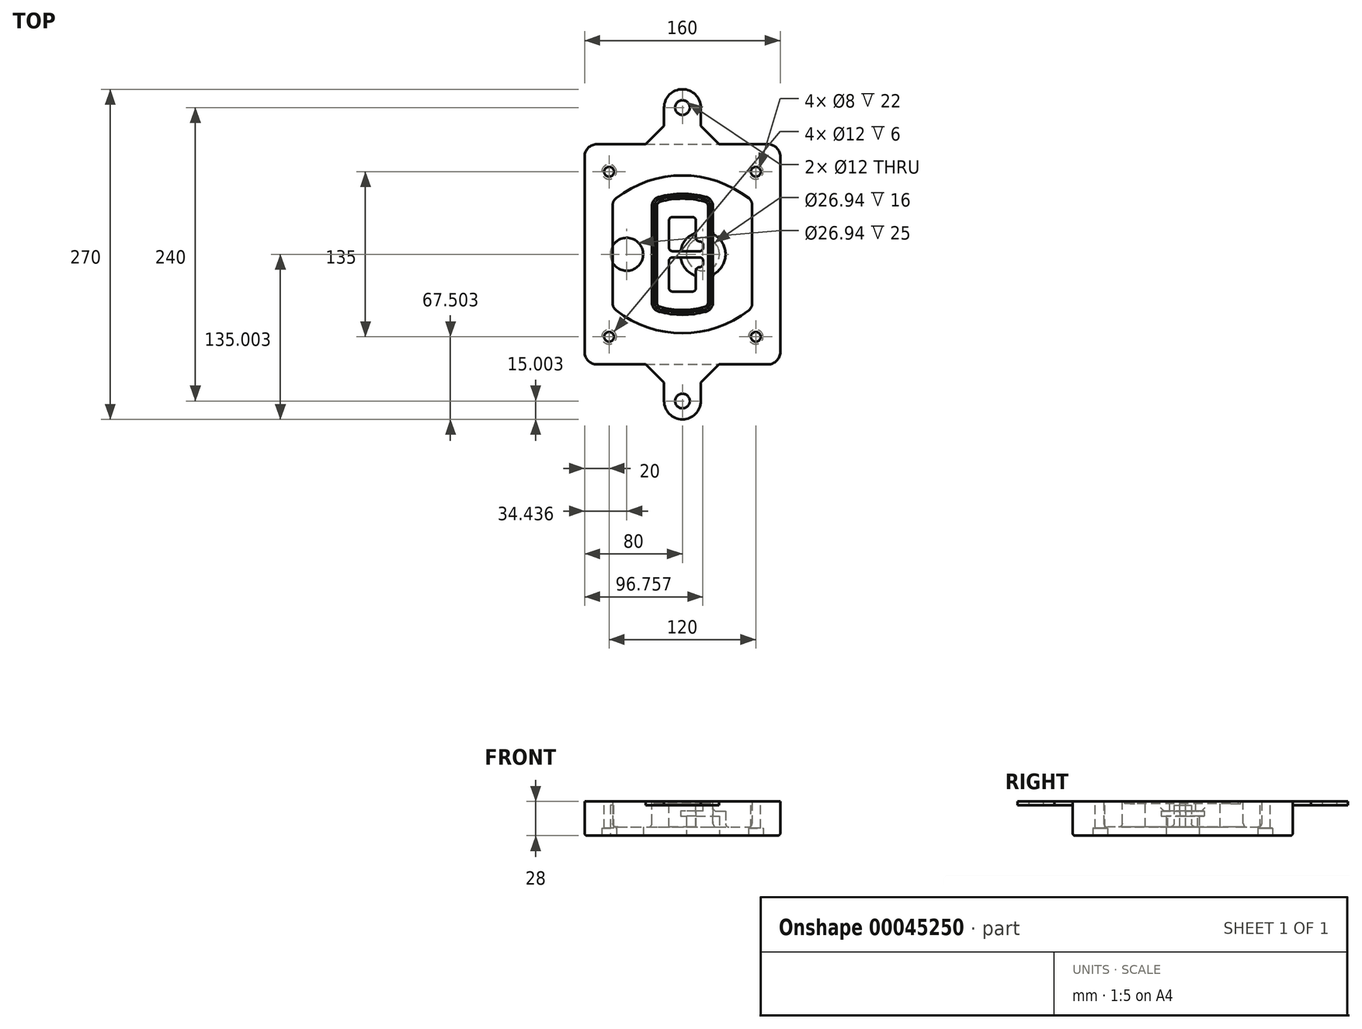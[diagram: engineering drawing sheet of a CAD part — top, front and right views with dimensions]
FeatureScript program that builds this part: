
annotation { "Feature Type Name" : "Feature", "Feature Type Description" : "" }
export const myFeature = defineFeature(function(context is Context, id is Id, definition is map)
    precondition{}
    {
        {
            var Q0;
            Q0=qCreatedBy(makeId("Top.planeOp"),FACE);
            var sketch = newSketch(context, id + "F0", { "sketchPlane" : qUnion([Q0])});
            skPoint(sketch, "E0.rect.middle", {"position": v(0, 0) * mm});
            skLineSegment(sketch, "E1.bottom", {"start": v(24.05, 28.38) * mm, "end": v(164.05, 28.38) * mm});
            skLineSegment(sketch, "E1.top", {"start": v(24.05, 208.38) * mm, "end": v(164.05, 208.38) * mm});
            skLineSegment(sketch, "E1.left", {"start": v(14.05, 38.38) * mm, "end": v(14.05, 198.38) * mm});
            skLineSegment(sketch, "E1.right", {"start": v(174.05, 38.38) * mm, "end": v(174.05, 198.38) * mm});
            skLineSegment(sketch, "E2", {"start": v(14.05, 208.38) * mm, "end": v(174.05, 28.38) * mm, "construction": true});
            skLineSegment(sketch, "E3", {"start": v(174.05, 208.38) * mm, "end": v(14.05, 28.38) * mm, "construction": true});
            skCircle(sketch, "E4", {"center": v(34.05, 185.88) * mm, "radius": 4 * mm});
            skCircle(sketch, "E5", {"center": v(154.05, 185.88) * mm, "radius": 4 * mm});
            skCircle(sketch, "E6", {"center": v(154.05, 50.88) * mm, "radius": 4 * mm});
            skCircle(sketch, "E7", {"center": v(34.05, 50.88) * mm, "radius": 4 * mm});
            skLineSegment(sketch, "E8", {"start": v(34.05, 185.88) * mm, "end": v(154.05, 185.88) * mm, "construction": true});
            skLineSegment(sketch, "E9", {"start": v(154.05, 185.88) * mm, "end": v(154.05, 50.88) * mm, "construction": true});
            skLineSegment(sketch, "E10", {"start": v(154.05, 50.88) * mm, "end": v(34.05, 50.88) * mm, "construction": true});
            skLineSegment(sketch, "E11", {"start": v(34.05, 50.88) * mm, "end": v(34.05, 185.88) * mm, "construction": true});
            skLineSegment(sketch, "E12", {"start": v(34.05, 158.68) * mm, "end": v(34.05, 78.09) * mm});
            skLineSegment(sketch, "E13", {"start": v(154.05, 158.68) * mm, "end": v(154.05, 78.09) * mm});
            skArc(sketch, "E14", {"start": v(150.2, 166.56) * mm, "mid": v(94.05, 185.88) * mm, "end": v(37.9, 166.56) * mm});
            skArc(sketch, "E15", {"start": v(37.9, 70.2) * mm, "mid": v(94.05, 50.88) * mm, "end": v(150.2, 70.2) * mm});
            skLineSegment(sketch, "E16", {"start": v(34.05, 118.38) * mm, "end": v(154.05, 118.38) * mm, "construction": true});
            skPoint(sketch, "E17.visualSharp", {"position": v(34.05, 73.38) * mm});
            skArc(sketch, "E17.filletArc", {"start": v(34.05, 78.09) * mm, "mid": v(35.06, 73.7) * mm, "end": v(37.9, 70.2) * mm});
            skPoint(sketch, "E18.visualSharp", {"position": v(34.05, 163.38) * mm});
            skArc(sketch, "E18.filletArc", {"start": v(37.9, 166.56) * mm, "mid": v(35.06, 163.06) * mm, "end": v(34.05, 158.68) * mm});
            skPoint(sketch, "E19.visualSharp", {"position": v(154.05, 163.38) * mm});
            skArc(sketch, "E19.filletArc", {"start": v(154.05, 158.68) * mm, "mid": v(153.04, 163.06) * mm, "end": v(150.2, 166.56) * mm});
            skPoint(sketch, "E20.visualSharp", {"position": v(154.05, 73.38) * mm});
            skArc(sketch, "E20.filletArc", {"start": v(150.2, 70.2) * mm, "mid": v(153.04, 73.7) * mm, "end": v(154.05, 78.09) * mm});
            skPoint(sketch, "E21.visualSharp", {"position": v(14.05, 208.38) * mm});
            skArc(sketch, "E21.filletArc", {"start": v(24.05, 208.38) * mm, "mid": v(16.98, 205.45) * mm, "end": v(14.05, 198.38) * mm});
            skPoint(sketch, "E22.visualSharp", {"position": v(174.05, 208.38) * mm});
            skArc(sketch, "E22.filletArc", {"start": v(174.05, 198.38) * mm, "mid": v(171.12, 205.45) * mm, "end": v(164.05, 208.38) * mm});
            skPoint(sketch, "E23.visualSharp", {"position": v(174.05, 28.38) * mm});
            skArc(sketch, "E23.filletArc", {"start": v(164.05, 28.38) * mm, "mid": v(171.12, 31.31) * mm, "end": v(174.05, 38.38) * mm});
            skPoint(sketch, "E24.visualSharp", {"position": v(14.05, 28.38) * mm});
            skArc(sketch, "E24.filletArc", {"start": v(14.05, 38.38) * mm, "mid": v(16.98, 31.31) * mm, "end": v(24.05, 28.38) * mm});
            skArc(sketch, "E25.0", {"start": v(151.05, 158.68) * mm, "mid": v(150.34, 161.75) * mm, "end": v(148.36, 164.2) * mm});
            skLineSegment(sketch, "E25.1", {"start": v(151.05, 158.68) * mm, "end": v(151.05, 78.09) * mm});
            skArc(sketch, "E25.2", {"start": v(148.36, 72.57) * mm, "mid": v(150.34, 75.02) * mm, "end": v(151.05, 78.09) * mm});
            skArc(sketch, "E25.3", {"start": v(39.74, 72.57) * mm, "mid": v(94.05, 53.88) * mm, "end": v(148.36, 72.57) * mm});
            skArc(sketch, "E25.4", {"start": v(37.05, 78.09) * mm, "mid": v(37.76, 75.02) * mm, "end": v(39.74, 72.57) * mm});
            skArc(sketch, "E25.5", {"start": v(148.36, 164.2) * mm, "mid": v(94.05, 182.88) * mm, "end": v(39.74, 164.2) * mm});
            skLineSegment(sketch, "E25.6", {"start": v(37.05, 158.68) * mm, "end": v(37.05, 78.09) * mm});
            skArc(sketch, "E25.7", {"start": v(39.74, 164.2) * mm, "mid": v(37.76, 161.75) * mm, "end": v(37.05, 158.68) * mm});
            skArc(sketch, "E26.0", {"start": v(35.43, 169.71) * mm, "mid": v(31.47, 164.82) * mm, "end": v(30.05, 158.68) * mm});
            skArc(sketch, "E26.1", {"start": v(152.67, 169.71) * mm, "mid": v(94.05, 189.88) * mm, "end": v(35.43, 169.71) * mm});
            skArc(sketch, "E26.2", {"start": v(158.05, 158.68) * mm, "mid": v(156.63, 164.82) * mm, "end": v(152.67, 169.71) * mm});
            skLineSegment(sketch, "E26.3", {"start": v(158.05, 158.68) * mm, "end": v(158.05, 78.09) * mm});
            skArc(sketch, "E26.4", {"start": v(152.67, 67.05) * mm, "mid": v(156.63, 71.95) * mm, "end": v(158.05, 78.09) * mm});
            skLineSegment(sketch, "E26.5", {"start": v(30.05, 158.68) * mm, "end": v(30.05, 78.09) * mm});
            skArc(sketch, "E26.6", {"start": v(35.43, 67.05) * mm, "mid": v(94.05, 46.88) * mm, "end": v(152.67, 67.05) * mm});
            skArc(sketch, "E26.7", {"start": v(30.05, 78.09) * mm, "mid": v(31.47, 71.95) * mm, "end": v(35.43, 67.05) * mm});
            skSolve(sketch);
        }
        {
            var Q0;
            Q0=makeQuery(id+"F0.imprint","IMPRINT",FACE,{"disambiguationData":[TD([[makeQuery(id+"F0.imprint","IMPRINT",EDGE,{"derivedFrom":sQuery(id+"F0.wireOp",EDGE,"E1.bottom")}),1.0]])]});
            var Q1;
            Q1=makeQuery(id+"F0.imprint","IMPRINT",FACE,{"disambiguationData":[TD([[makeQuery(id+"F0.imprint","IMPRINT",EDGE,{"derivedFrom":sQuery(id+"F0.wireOp",EDGE,"E12")}),1.0]])]});
            var Q2;
            Q2=makeQuery(id+"F0.imprint","IMPRINT",FACE,{"disambiguationData":[TD([[makeQuery(id+"F0.imprint","IMPRINT",EDGE,{"derivedFrom":sQuery(id+"F0.wireOp",EDGE,"E25.0")}),1.0]])]});
            var Q3;
            Q3=makeQuery(id+"F0.imprint","IMPRINT",FACE,{"disambiguationData":[TD([[makeQuery(id+"F0.imprint","IMPRINT",EDGE,{"derivedFrom":sQuery(id+"F0.wireOp",EDGE,"E12")}),-1.0]])]});
            extrude(context, id + "F1", {"entities" : qUnion([Q0, Q1, Q2, Q3]), "oppositeDirection" : true, "depth" : 25 * mm});
        }
        {
            var Q0;
            Q0=makeQuery(id+"F0.imprint","IMPRINT",FACE,{"disambiguationData":[TD([[makeQuery(id+"F0.imprint","IMPRINT",EDGE,{"derivedFrom":sQuery(id+"F0.wireOp",EDGE,"E12")}),1.0]])]});
            extrude(context, id + "F2", {"entities" : qUnion([Q0]), "operationType" : NewBodyOperationType.ADD, "depth" : 3 * mm});
        }
        {
            var Q0;
            Q0=makeQuery(id+"F0.imprint","IMPRINT",FACE,{"disambiguationData":[TD([[makeQuery(id+"F0.imprint","IMPRINT",EDGE,{"derivedFrom":sQuery(id+"F0.wireOp",EDGE,"E25.0")}),1.0]])]});
            extrude(context, id + "F3", {"entities" : qUnion([Q0]), "operationType" : NewBodyOperationType.REMOVE, "oppositeDirection" : true, "depth" : 18 * mm});
        }
        {
            var Q0;
            Q0=makeQuery(id+"F2.opExtrude","CAP_FACE",FACE,{"disambiguationData":[OSD([sQuery(id+"F0.wireOp",EDGE,"E12"),sQuery(id+"F0.wireOp",EDGE,"E13"),sQuery(id+"F0.wireOp",EDGE,"E14"),sQuery(id+"F0.wireOp",EDGE,"E15"),sQuery(id+"F0.wireOp",EDGE,"E17.filletArc"),sQuery(id+"F0.wireOp",EDGE,"E18.filletArc"),sQuery(id+"F0.wireOp",EDGE,"E19.filletArc"),sQuery(id+"F0.wireOp",EDGE,"E20.filletArc"),sQuery(id+"F0.wireOp",EDGE,"E25.0"),sQuery(id+"F0.wireOp",EDGE,"E25.1"),sQuery(id+"F0.wireOp",EDGE,"E25.2"),sQuery(id+"F0.wireOp",EDGE,"E25.3"),sQuery(id+"F0.wireOp",EDGE,"E25.4"),sQuery(id+"F0.wireOp",EDGE,"E25.5"),sQuery(id+"F0.wireOp",EDGE,"E25.6"),sQuery(id+"F0.wireOp",EDGE,"E25.7")])],"isStart":false});
            var sketch = newSketch(context, id + "F4", { "sketchPlane" : qUnion([Q0])});
            skArc(sketch, "E27.0", {"start": v(74.97, 71.41) * mm, "mid": v(94.05, 68.88) * mm, "end": v(113.13, 71.41) * mm});
            skArc(sketch, "E28.0", {"start": v(113.13, 165.35) * mm, "mid": v(94.05, 167.88) * mm, "end": v(74.97, 165.35) * mm});
            skLineSegment(sketch, "E29", {"start": v(69.05, 157.63) * mm, "end": v(69.05, 79.14) * mm});
            skLineSegment(sketch, "E30", {"start": v(119.05, 157.63) * mm, "end": v(119.05, 79.14) * mm});
            skLineSegment(sketch, "E31", {"start": v(69.05, 163.48) * mm, "end": v(119.05, 163.48) * mm, "construction": true});
            skLineSegment(sketch, "E32", {"start": v(69.05, 73.28) * mm, "end": v(119.05, 73.28) * mm, "construction": true});
            skPoint(sketch, "E33.visualSharp", {"position": v(69.05, 163.48) * mm});
            skArc(sketch, "E33.filletArc", {"start": v(74.97, 165.35) * mm, "mid": v(70.7, 162.5) * mm, "end": v(69.05, 157.63) * mm});
            skPoint(sketch, "E34.visualSharp", {"position": v(119.05, 163.48) * mm});
            skArc(sketch, "E34.filletArc", {"start": v(119.05, 157.63) * mm, "mid": v(117.4, 162.5) * mm, "end": v(113.13, 165.35) * mm});
            skPoint(sketch, "E35.visualSharp", {"position": v(119.05, 73.28) * mm});
            skArc(sketch, "E35.filletArc", {"start": v(113.13, 71.41) * mm, "mid": v(117.4, 74.27) * mm, "end": v(119.05, 79.14) * mm});
            skPoint(sketch, "E36.visualSharp", {"position": v(69.05, 73.28) * mm});
            skArc(sketch, "E36.filletArc", {"start": v(69.05, 79.14) * mm, "mid": v(70.7, 74.27) * mm, "end": v(74.97, 71.41) * mm});
            skArc(sketch, "E37.0", {"start": v(148.36, 164.2) * mm, "mid": v(94.05, 182.88) * mm, "end": v(39.74, 164.2) * mm});
            skArc(sketch, "E37.1", {"start": v(39.74, 164.2) * mm, "mid": v(37.76, 161.75) * mm, "end": v(37.05, 158.68) * mm});
            skLineSegment(sketch, "E37.2", {"start": v(37.05, 158.68) * mm, "end": v(37.05, 78.09) * mm});
            skArc(sketch, "E37.3", {"start": v(37.05, 78.09) * mm, "mid": v(37.76, 75.02) * mm, "end": v(39.74, 72.57) * mm});
            skArc(sketch, "E37.4", {"start": v(39.74, 72.57) * mm, "mid": v(94.05, 53.88) * mm, "end": v(148.36, 72.57) * mm});
            skArc(sketch, "E37.5", {"start": v(148.36, 72.57) * mm, "mid": v(150.34, 75.02) * mm, "end": v(151.05, 78.09) * mm});
            skLineSegment(sketch, "E37.6", {"start": v(151.05, 158.68) * mm, "end": v(151.05, 78.09) * mm});
            skArc(sketch, "E37.7", {"start": v(151.05, 158.68) * mm, "mid": v(150.34, 161.75) * mm, "end": v(148.36, 164.2) * mm});
            skLineSegment(sketch, "E38.0", {"start": v(117.05, 157.63) * mm, "end": v(117.05, 79.14) * mm});
            skArc(sketch, "E38.1", {"start": v(112.61, 73.34) * mm, "mid": v(115.81, 75.49) * mm, "end": v(117.05, 79.14) * mm});
            skArc(sketch, "E38.2", {"start": v(75.49, 73.34) * mm, "mid": v(94.05, 70.88) * mm, "end": v(112.61, 73.34) * mm});
            skArc(sketch, "E38.3", {"start": v(71.05, 79.14) * mm, "mid": v(72.29, 75.49) * mm, "end": v(75.49, 73.34) * mm});
            skLineSegment(sketch, "E38.4", {"start": v(71.05, 157.63) * mm, "end": v(71.05, 79.14) * mm});
            skArc(sketch, "E38.5", {"start": v(117.05, 157.63) * mm, "mid": v(115.81, 161.28) * mm, "end": v(112.61, 163.42) * mm});
            skArc(sketch, "E38.6", {"start": v(75.49, 163.42) * mm, "mid": v(72.29, 161.28) * mm, "end": v(71.05, 157.63) * mm});
            skArc(sketch, "E38.7", {"start": v(112.61, 163.42) * mm, "mid": v(94.05, 165.88) * mm, "end": v(75.49, 163.42) * mm});
            skArc(sketch, "E39.0", {"start": v(115.05, 157.63) * mm, "mid": v(114.23, 160.06) * mm, "end": v(112.1, 161.5) * mm});
            skLineSegment(sketch, "E39.1", {"start": v(115.05, 157.63) * mm, "end": v(115.05, 79.14) * mm});
            skArc(sketch, "E39.2", {"start": v(112.1, 75.27) * mm, "mid": v(114.23, 76.7) * mm, "end": v(115.05, 79.14) * mm});
            skArc(sketch, "E39.3", {"start": v(76, 75.27) * mm, "mid": v(94.05, 72.88) * mm, "end": v(112.1, 75.27) * mm});
            skArc(sketch, "E39.4", {"start": v(73.05, 79.14) * mm, "mid": v(73.87, 76.7) * mm, "end": v(76, 75.27) * mm});
            skArc(sketch, "E39.5", {"start": v(112.1, 161.5) * mm, "mid": v(94.05, 163.88) * mm, "end": v(76, 161.5) * mm});
            skLineSegment(sketch, "E39.6", {"start": v(73.05, 157.63) * mm, "end": v(73.05, 79.14) * mm});
            skArc(sketch, "E39.7", {"start": v(76, 161.5) * mm, "mid": v(73.87, 160.06) * mm, "end": v(73.05, 157.63) * mm});
            skLineSegment(sketch, "E40", {"start": v(69.05, 118.38) * mm, "end": v(119.05, 118.38) * mm, "construction": true});
            skLineSegment(sketch, "E41", {"start": v(83.05, 123.88) * mm, "end": v(83.05, 145.88) * mm});
            skLineSegment(sketch, "E42", {"start": v(86.05, 148.88) * mm, "end": v(102.05, 148.88) * mm});
            skLineSegment(sketch, "E43", {"start": v(105.05, 145.88) * mm, "end": v(105.05, 131.88) * mm});
            skLineSegment(sketch, "E44", {"start": v(108.05, 128.88) * mm, "end": v(108.05, 128.88) * mm});
            skLineSegment(sketch, "E45", {"start": v(111.05, 125.88) * mm, "end": v(111.05, 123.88) * mm});
            skLineSegment(sketch, "E46", {"start": v(108.05, 120.88) * mm, "end": v(86.05, 120.88) * mm});
            skPoint(sketch, "E47.visualSharp", {"position": v(83.05, 148.88) * mm});
            skArc(sketch, "E47.filletArc", {"start": v(86.05, 148.88) * mm, "mid": v(83.93, 148) * mm, "end": v(83.05, 145.88) * mm});
            skPoint(sketch, "E48.visualSharp", {"position": v(105.05, 148.88) * mm});
            skArc(sketch, "E48.filletArc", {"start": v(105.05, 145.88) * mm, "mid": v(104.17, 148) * mm, "end": v(102.05, 148.88) * mm});
            skPoint(sketch, "E49.visualSharp", {"position": v(105.05, 128.88) * mm});
            skArc(sketch, "E49.filletArc", {"start": v(105.05, 131.88) * mm, "mid": v(105.93, 129.76) * mm, "end": v(108.05, 128.88) * mm});
            skPoint(sketch, "E50.visualSharp", {"position": v(111.05, 128.88) * mm});
            skArc(sketch, "E50.filletArc", {"start": v(111.05, 125.88) * mm, "mid": v(110.17, 128) * mm, "end": v(108.05, 128.88) * mm});
            skPoint(sketch, "E51.visualSharp", {"position": v(111.05, 120.88) * mm});
            skArc(sketch, "E51.filletArc", {"start": v(108.05, 120.88) * mm, "mid": v(110.17, 121.76) * mm, "end": v(111.05, 123.88) * mm});
            skPoint(sketch, "E52.visualSharp", {"position": v(83.05, 120.88) * mm});
            skArc(sketch, "E52.filletArc", {"start": v(83.05, 123.88) * mm, "mid": v(83.93, 121.76) * mm, "end": v(86.05, 120.88) * mm});
            skLineSegment(sketch, "E53.0.MirrorCS", {"start": v(108.05, 115.88) * mm, "end": v(86.05, 115.88) * mm});
            skArc(sketch, "E54.0.MirrorCS", {"start": v(83.05, 112.88) * mm, "mid": v(83.93, 115) * mm, "end": v(86.05, 115.88) * mm});
            skLineSegment(sketch, "E55.0.MirrorCS", {"start": v(83.05, 112.88) * mm, "end": v(83.05, 90.88) * mm});
            skArc(sketch, "E56.0.MirrorCS", {"start": v(86.05, 87.88) * mm, "mid": v(83.93, 88.76) * mm, "end": v(83.05, 90.88) * mm});
            skLineSegment(sketch, "E57.0.MirrorCS", {"start": v(86.05, 87.88) * mm, "end": v(102.05, 87.88) * mm});
            skArc(sketch, "E58.0.MirrorCS", {"start": v(105.05, 90.88) * mm, "mid": v(104.17, 88.76) * mm, "end": v(102.05, 87.88) * mm});
            skLineSegment(sketch, "E59.0.MirrorCS", {"start": v(105.05, 90.88) * mm, "end": v(105.05, 104.88) * mm});
            skArc(sketch, "E60.0.MirrorCS", {"start": v(105.05, 104.88) * mm, "mid": v(105.93, 107) * mm, "end": v(108.05, 107.88) * mm});
            skArc(sketch, "E61.0.MirrorCS", {"start": v(111.05, 110.88) * mm, "mid": v(110.17, 108.76) * mm, "end": v(108.05, 107.88) * mm});
            skLineSegment(sketch, "E62.0.MirrorCS", {"start": v(111.05, 110.88) * mm, "end": v(111.05, 112.88) * mm});
            skArc(sketch, "E63.0.MirrorCS", {"start": v(108.05, 115.88) * mm, "mid": v(110.17, 115) * mm, "end": v(111.05, 112.88) * mm});
            skSolve(sketch);
        }
        {
            var Q0;
            Q0=makeQuery(id+"F4.imprint","IMPRINT",FACE,{"disambiguationData":[TD([[makeQuery(id+"F4.imprint","IMPRINT",EDGE,{"derivedFrom":sQuery(id+"F4.wireOp",EDGE,"E27.0")}),1.0]])]});
            var Q1;
            Q1=makeQuery(id+"F4.imprint","IMPRINT",FACE,{"disambiguationData":[TD([[makeQuery(id+"F4.imprint","IMPRINT",EDGE,{"derivedFrom":sQuery(id+"F4.wireOp",EDGE,"E38.0")}),-1.0]])]});
            var Q2;
            Q2=makeQuery(id+"F4.imprint","IMPRINT",FACE,{"disambiguationData":[TD([[makeQuery(id+"F4.imprint","IMPRINT",EDGE,{"derivedFrom":sQuery(id+"F4.wireOp",EDGE,"E39.0")}),1.0]])]});
            extrude(context, id + "F5", {"entities" : qUnion([Q0, Q1, Q2]), "operationType" : NewBodyOperationType.ADD, "endBound" : BoundingType.UP_TO_NEXT, "oppositeDirection" : true, "depth" : 25 * mm});
        }
        {
            var Q0;
            Q0=makeQuery(id+"F4.imprint","IMPRINT",FACE,{"disambiguationData":[TD([[makeQuery(id+"F4.imprint","IMPRINT",EDGE,{"derivedFrom":sQuery(id+"F4.wireOp",EDGE,"E38.0")}),-1.0]])]});
            extrude(context, id + "F6", {"entities" : qUnion([Q0]), "operationType" : NewBodyOperationType.REMOVE, "oppositeDirection" : true, "depth" : 2 * mm});
        }
        {
            var Q0;
            Q0=makeQuery(id+"F1.opExtrude","CAP_FACE",FACE,{"disambiguationData":[OSD([sQuery(id+"F0.wireOp",EDGE,"E1.bottom"),sQuery(id+"F0.wireOp",EDGE,"E1.top"),sQuery(id+"F0.wireOp",EDGE,"E1.left"),sQuery(id+"F0.wireOp",EDGE,"E1.right"),sQuery(id+"F0.wireOp",EDGE,"E4"),sQuery(id+"F0.wireOp",EDGE,"E5"),sQuery(id+"F0.wireOp",EDGE,"E6"),sQuery(id+"F0.wireOp",EDGE,"E7"),sQuery(id+"F0.wireOp",EDGE,"E21.filletArc"),sQuery(id+"F0.wireOp",EDGE,"E22.filletArc"),sQuery(id+"F0.wireOp",EDGE,"E23.filletArc"),sQuery(id+"F0.wireOp",EDGE,"E24.filletArc")])],"isStart":false});
            var sketch = newSketch(context, id + "F7", { "sketchPlane" : qUnion([Q0])});
            skCircle(sketch, "E64", {"center": v(110.8, -118.38) * mm, "radius": 13.47 * mm});
            skCircle(sketch, "E65", {"center": v(48.49, -118.38) * mm, "radius": 13.47 * mm});
            skLineSegment(sketch, "E66", {"start": v(174.05, -118.38) * mm, "end": v(14.05, -118.38) * mm});
            skCircle(sketch, "E67", {"center": v(110.8, -118.38) * mm, "radius": 18.47 * mm});
            skCircle(sketch, "E68", {"center": v(154.05, -185.88) * mm, "radius": 6 * mm});
            skCircle(sketch, "E69", {"center": v(34.05, -185.88) * mm, "radius": 6 * mm});
            skCircle(sketch, "E70", {"center": v(34.05, -50.88) * mm, "radius": 6 * mm});
            skCircle(sketch, "E71", {"center": v(154.05, -50.88) * mm, "radius": 6 * mm});
            skSolve(sketch);
        }
        {
            var Q0;
            {var subQ1=sQuery(id+"F7.wireOp",EDGE,"E66");var subQ4=sQuery(id+"F7.wireOp",EDGE,"E64");var subQ6=makeQuery(id+"F7.imprint","INTERSECT",VERTEX,{"disambiguationData":[OD(0.0)],"derivedFrom":[subQ4,subQ1]});Q0=makeQuery(id+"F7.imprint","IMPRINT",FACE,{"disambiguationData":[TD([[makeQuery(id+"F7.imprint","IMPRINT",EDGE,{"disambiguationData":[TD([[subQ6,-1.0]])],"derivedFrom":subQ4}),-1.0]])]});}
            var Q1;
            {var subQ0=sQuery(id+"F7.wireOp",EDGE,"E66");var subQ1=sQuery(id+"F7.wireOp",EDGE,"E64");var subQ3=makeQuery(id+"F7.imprint","INTERSECT",VERTEX,{"disambiguationData":[OD(0.0)],"derivedFrom":[subQ1,subQ0]});Q1=makeQuery(id+"F7.imprint","IMPRINT",FACE,{"disambiguationData":[TD([[makeQuery(id+"F7.imprint","IMPRINT",EDGE,{"disambiguationData":[TD([[subQ3,-1.0]])],"derivedFrom":subQ1}),1.0]])]});}
            var Q2;
            {var subQ0=sQuery(id+"F7.wireOp",EDGE,"E66");var subQ1=sQuery(id+"F7.wireOp",EDGE,"E64");var subQ3=makeQuery(id+"F7.imprint","INTERSECT",VERTEX,{"disambiguationData":[OD(0.0)],"derivedFrom":[subQ1,subQ0]});Q2=makeQuery(id+"F7.imprint","IMPRINT",FACE,{"disambiguationData":[TD([[makeQuery(id+"F7.imprint","IMPRINT",EDGE,{"disambiguationData":[TD([[subQ3,1.0]])],"derivedFrom":subQ1}),1.0]])]});}
            var Q3;
            {var subQ1=sQuery(id+"F7.wireOp",EDGE,"E66");var subQ4=sQuery(id+"F7.wireOp",EDGE,"E64");var subQ6=makeQuery(id+"F7.imprint","INTERSECT",VERTEX,{"disambiguationData":[OD(0.0)],"derivedFrom":[subQ4,subQ1]});Q3=makeQuery(id+"F7.imprint","IMPRINT",FACE,{"disambiguationData":[TD([[makeQuery(id+"F7.imprint","IMPRINT",EDGE,{"disambiguationData":[TD([[subQ6,1.0]])],"derivedFrom":subQ4}),-1.0]])]});}
            extrude(context, id + "F8", {"entities" : qUnion([Q0, Q1, Q2, Q3]), "operationType" : NewBodyOperationType.ADD, "oppositeDirection" : true, "depth" : 20 * mm});
        }
        {
            var Q0;
            {var subQ0=sQuery(id+"F7.wireOp",EDGE,"E66");var subQ1=sQuery(id+"F7.wireOp",EDGE,"E64");var subQ3=makeQuery(id+"F7.imprint","INTERSECT",VERTEX,{"disambiguationData":[OD(0.0)],"derivedFrom":[subQ1,subQ0]});Q0=makeQuery(id+"F7.imprint","IMPRINT",FACE,{"disambiguationData":[TD([[makeQuery(id+"F7.imprint","IMPRINT",EDGE,{"disambiguationData":[TD([[subQ3,-1.0]])],"derivedFrom":subQ1}),1.0]])]});}
            var Q1;
            {var subQ0=sQuery(id+"F7.wireOp",EDGE,"E66");var subQ1=sQuery(id+"F7.wireOp",EDGE,"E64");var subQ3=makeQuery(id+"F7.imprint","INTERSECT",VERTEX,{"disambiguationData":[OD(0.0)],"derivedFrom":[subQ1,subQ0]});Q1=makeQuery(id+"F7.imprint","IMPRINT",FACE,{"disambiguationData":[TD([[makeQuery(id+"F7.imprint","IMPRINT",EDGE,{"disambiguationData":[TD([[subQ3,1.0]])],"derivedFrom":subQ1}),1.0]])]});}
            extrude(context, id + "F9", {"entities" : qUnion([Q0, Q1]), "operationType" : NewBodyOperationType.REMOVE, "oppositeDirection" : true, "depth" : 16 * mm});
        }
        {
            var Q0;
            {var subQ0=sQuery(id+"F7.wireOp",EDGE,"E66");var subQ1=sQuery(id+"F7.wireOp",EDGE,"E65");var subQ3=makeQuery(id+"F7.imprint","INTERSECT",VERTEX,{"disambiguationData":[OD(0.0)],"derivedFrom":[subQ1,subQ0]});Q0=makeQuery(id+"F7.imprint","IMPRINT",FACE,{"disambiguationData":[TD([[makeQuery(id+"F7.imprint","IMPRINT",EDGE,{"disambiguationData":[TD([[subQ3,-1.0]])],"derivedFrom":subQ1}),1.0]])]});}
            var Q1;
            {var subQ0=sQuery(id+"F7.wireOp",EDGE,"E66");var subQ1=sQuery(id+"F7.wireOp",EDGE,"E65");var subQ3=makeQuery(id+"F7.imprint","INTERSECT",VERTEX,{"disambiguationData":[OD(0.0)],"derivedFrom":[subQ1,subQ0]});Q1=makeQuery(id+"F7.imprint","IMPRINT",FACE,{"disambiguationData":[TD([[makeQuery(id+"F7.imprint","IMPRINT",EDGE,{"disambiguationData":[TD([[subQ3,1.0]])],"derivedFrom":subQ1}),1.0]])]});}
            extrude(context, id + "F10", {"entities" : qUnion([Q0, Q1]), "operationType" : NewBodyOperationType.REMOVE, "oppositeDirection" : true, "depth" : 25 * mm});
        }
        {
            var Q0;
            Q0=makeQuery(id+"F7.imprint","IMPRINT",FACE,{"disambiguationData":[TD([[makeQuery(id+"F7.imprint","IMPRINT",EDGE,{"derivedFrom":sQuery(id+"F7.wireOp",EDGE,"E68")}),1.0]])]});
            var Q1;
            Q1=makeQuery(id+"F7.imprint","IMPRINT",FACE,{"disambiguationData":[TD([[makeQuery(id+"F7.imprint","IMPRINT",EDGE,{"derivedFrom":makeQuery(id+"F1.opExtrude","CAP_EDGE",EDGE,{"disambiguationData":[OSD([sQuery(id+"F0.wireOp",EDGE,"E5")])],"isStart":false})}),-1.0]])]});
            var Q2;
            Q2=makeQuery(id+"F7.imprint","IMPRINT",FACE,{"disambiguationData":[TD([[makeQuery(id+"F7.imprint","IMPRINT",EDGE,{"derivedFrom":sQuery(id+"F7.wireOp",EDGE,"E69")}),1.0]])]});
            var Q3;
            Q3=makeQuery(id+"F7.imprint","IMPRINT",FACE,{"disambiguationData":[TD([[makeQuery(id+"F7.imprint","IMPRINT",EDGE,{"derivedFrom":makeQuery(id+"F1.opExtrude","CAP_EDGE",EDGE,{"disambiguationData":[OSD([sQuery(id+"F0.wireOp",EDGE,"E4")])],"isStart":false})}),-1.0]])]});
            var Q4;
            Q4=makeQuery(id+"F7.imprint","IMPRINT",FACE,{"disambiguationData":[TD([[makeQuery(id+"F7.imprint","IMPRINT",EDGE,{"derivedFrom":sQuery(id+"F7.wireOp",EDGE,"E70")}),1.0]])]});
            var Q5;
            Q5=makeQuery(id+"F7.imprint","IMPRINT",FACE,{"disambiguationData":[TD([[makeQuery(id+"F7.imprint","IMPRINT",EDGE,{"derivedFrom":makeQuery(id+"F1.opExtrude","CAP_EDGE",EDGE,{"disambiguationData":[OSD([sQuery(id+"F0.wireOp",EDGE,"E7")])],"isStart":false})}),-1.0]])]});
            var Q6;
            Q6=makeQuery(id+"F7.imprint","IMPRINT",FACE,{"disambiguationData":[TD([[makeQuery(id+"F7.imprint","IMPRINT",EDGE,{"derivedFrom":sQuery(id+"F7.wireOp",EDGE,"E71")}),1.0]])]});
            var Q7;
            Q7=makeQuery(id+"F7.imprint","IMPRINT",FACE,{"disambiguationData":[TD([[makeQuery(id+"F7.imprint","IMPRINT",EDGE,{"derivedFrom":makeQuery(id+"F1.opExtrude","CAP_EDGE",EDGE,{"disambiguationData":[OSD([sQuery(id+"F0.wireOp",EDGE,"E6")])],"isStart":false})}),-1.0]])]});
            extrude(context, id + "F11", {"entities" : qUnion([Q0, Q1, Q2, Q3, Q4, Q5, Q6, Q7]), "operationType" : NewBodyOperationType.REMOVE, "oppositeDirection" : true, "depth" : 6 * mm});
        }
        {
            var Q0;
            Q0=makeQuery(id+"F9.boolean.opBoolean","COPY",FACE,{"derivedFrom":makeQuery(id+"F9.opExtrude","CAP_FACE",FACE,{"disambiguationData":[OSD([sQuery(id+"F7.wireOp",EDGE,"E64")])],"isStart":false})});
            var sketch = newSketch(context, id + "F12", { "sketchPlane" : qUnion([Q0])});
            skArc(sketch, "E72.0", {"start": v(105.05, -100.83) * mm, "mid": v(96.62, -106.56) * mm, "end": v(92.5, -115.88) * mm});
            skArc(sketch, "E72.1", {"start": v(92.5, -120.88) * mm, "mid": v(96.62, -130.2) * mm, "end": v(105.05, -135.93) * mm});
            skLineSegment(sketch, "E73", {"start": v(92.5, -120.88) * mm, "end": v(108.05, -120.88) * mm});
            skLineSegment(sketch, "E74.0", {"start": v(108.05, -115.88) * mm, "end": v(92.5, -115.88) * mm});
            skArc(sketch, "E74.1", {"start": v(108.05, -115.88) * mm, "mid": v(110.17, -115) * mm, "end": v(111.05, -112.88) * mm});
            skLineSegment(sketch, "E74.2", {"start": v(111.05, -110.88) * mm, "end": v(111.05, -112.88) * mm});
            skArc(sketch, "E74.3", {"start": v(111.05, -110.88) * mm, "mid": v(110.17, -108.76) * mm, "end": v(108.05, -107.88) * mm});
            skArc(sketch, "E74.4", {"start": v(105.05, -104.88) * mm, "mid": v(105.93, -107) * mm, "end": v(108.05, -107.88) * mm});
            skLineSegment(sketch, "E74.5", {"start": v(105.05, -100.83) * mm, "end": v(105.05, -104.88) * mm});
            skLineSegment(sketch, "E74.7", {"start": v(108.05, -120.88) * mm, "end": v(92.5, -120.88) * mm});
            skArc(sketch, "E74.8", {"start": v(108.05, -120.88) * mm, "mid": v(110.17, -121.76) * mm, "end": v(111.05, -123.88) * mm});
            skLineSegment(sketch, "E74.9", {"start": v(111.05, -125.88) * mm, "end": v(111.05, -123.88) * mm});
            skArc(sketch, "E74.10", {"start": v(111.05, -125.88) * mm, "mid": v(110.17, -128) * mm, "end": v(108.05, -128.88) * mm});
            skArc(sketch, "E74.11", {"start": v(105.05, -131.88) * mm, "mid": v(105.93, -129.76) * mm, "end": v(108.05, -128.88) * mm});
            skLineSegment(sketch, "E74.12", {"start": v(105.05, -135.93) * mm, "end": v(105.05, -131.88) * mm});
            skPoint(sketch, "E75.orphan", {"position": v(105.05, -145.88) * mm});
            skPoint(sketch, "E76.orphan", {"position": v(86.05, -120.88) * mm});
            skPoint(sketch, "E77.orphan", {"position": v(86.05, -115.88) * mm});
            skPoint(sketch, "E78.orphan", {"position": v(105.05, -90.88) * mm});
            skSolve(sketch);
        }
        {
            var Q0;
            {var subQ7=sQuery(id+"F12.wireOp",EDGE,"E72.0");var subQ14=sQuery(id+"F12.wireOp",EDGE,"E72.1");var subQ16=sQuery(id+"F12.wireOp",EDGE,"E74.1");var subQ18=sQuery(id+"F12.wireOp",EDGE,"E74.8");Q0=qUnion([makeQuery(id+"F12.imprint","IMPRINT",FACE,{"disambiguationData":[TD([[makeQuery(id+"F12.imprint","IMPRINT",EDGE,{"derivedFrom":subQ7}),1.0]])]}),makeQuery(id+"F12.imprint","IMPRINT",FACE,{"disambiguationData":[TD([[makeQuery(id+"F12.imprint","IMPRINT",EDGE,{"derivedFrom":subQ14}),1.0]])]}),makeQuery(id+"F12.imprint","IMPRINT",FACE,{"disambiguationData":[TD([[makeQuery(id+"F12.imprint","IMPRINT",EDGE,{"derivedFrom":subQ16}),1.0]])]}),makeQuery(id+"F12.imprint","IMPRINT",FACE,{"disambiguationData":[TD([[makeQuery(id+"F12.imprint","IMPRINT",EDGE,{"derivedFrom":subQ18}),-1.0]])]})]);}
            var Q1;
            Q1=makeQuery(id+"F5.boolean.opBoolean","SPLIT",FACE,{"disambiguationData":[TD([makeQuery(id+"F5.opExtrude","SWEPT_FACE",FACE,{"disambiguationData":[OSD([sQuery(id+"F4.wireOp",EDGE,"E41")])]})])],"derivedFrom":makeQuery(id+"F3.boolean.opBoolean","COPY",FACE,{"derivedFrom":makeQuery(id+"F3.opExtrude","CAP_FACE",FACE,{"disambiguationData":[OSD([sQuery(id+"F0.wireOp",EDGE,"E25.0"),sQuery(id+"F0.wireOp",EDGE,"E25.1"),sQuery(id+"F0.wireOp",EDGE,"E25.2"),sQuery(id+"F0.wireOp",EDGE,"E25.3"),sQuery(id+"F0.wireOp",EDGE,"E25.4"),sQuery(id+"F0.wireOp",EDGE,"E25.5"),sQuery(id+"F0.wireOp",EDGE,"E25.6"),sQuery(id+"F0.wireOp",EDGE,"E25.7")])],"isStart":false})})});
            extrude(context, id + "F13", {"entities" : qUnion([Q0]), "operationType" : NewBodyOperationType.REMOVE, "endBound" : BoundingType.UP_TO_SURFACE, "endBoundEntityFace" : qUnion([Q1]), "depth" : 25 * mm});
        }
        {
            var Q0;
            Q0=makeQuery(id+"F3.boolean.opBoolean","COPY",EDGE,{"derivedFrom":makeQuery(id+"F3.opExtrude","CAP_EDGE",EDGE,{"disambiguationData":[OSD([sQuery(id+"F0.wireOp",EDGE,"E25.6")])],"isStart":false})});
            var Q1;
            Q1=makeQuery(id+"F8.boolean.opBoolean","INTERSECT",EDGE,{"derivedFrom":[makeQuery(id+"F5.opExtrude","SWEPT_FACE",FACE,{"disambiguationData":[OSD([sQuery(id+"F4.wireOp",EDGE,"E30")])]}),makeQuery(id+"F8.opExtrude","CAP_FACE",FACE,{"disambiguationData":[OSD([sQuery(id+"F7.wireOp",EDGE,"E67")])],"isStart":false})]});
            var Q2;
            Q2=makeQuery(id+"F8.boolean.opBoolean","INTERSECT",EDGE,{"disambiguationData":[OD(1.0)],"derivedFrom":[makeQuery(id+"F5.opExtrude","SWEPT_FACE",FACE,{"disambiguationData":[OSD([sQuery(id+"F4.wireOp",EDGE,"E30")])]}),makeQuery(id+"F8.opExtrude","SWEPT_FACE",FACE,{"disambiguationData":[OSD([sQuery(id+"F7.wireOp",EDGE,"E67")])]})]});
            var Q3;
            {var subQ0=sQuery(id+"F4.wireOp",EDGE,"E30");Q3=makeQuery(id+"F8.boolean.opBoolean","SPLIT",EDGE,{"disambiguationData":[TD([makeQuery(id+"F5.opExtrude","SWEPT_FACE",FACE,{"disambiguationData":[OSD([sQuery(id+"F4.wireOp",EDGE,"E35.filletArc")])]})])],"derivedFrom":makeQuery(id+"F5.opExtrude","CAP_EDGE",EDGE,{"disambiguationData":[OSD([subQ0])],"isStart":false})});}
            var Q4;
            {var subQ0=sQuery(id+"F0.wireOp",EDGE,"E25.7");var subQ1=sQuery(id+"F0.wireOp",EDGE,"E25.1");var subQ2=sQuery(id+"F0.wireOp",EDGE,"E25.6");var subQ3=sQuery(id+"F0.wireOp",EDGE,"E25.5");var subQ4=sQuery(id+"F0.wireOp",EDGE,"E25.4");var subQ5=sQuery(id+"F0.wireOp",EDGE,"E25.0");var subQ6=sQuery(id+"F0.wireOp",EDGE,"E25.2");var subQ7=sQuery(id+"F0.wireOp",EDGE,"E25.3");Q4=makeQuery(id+"F8.boolean.opBoolean","INTERSECT",EDGE,{"derivedFrom":[makeQuery(id+"F5.boolean.opBoolean","SPLIT",FACE,{"disambiguationData":[TD([makeQuery(id+"F2.opExtrude","SWEPT_FACE",FACE,{"disambiguationData":[OSD([subQ5])]})])],"derivedFrom":makeQuery(id+"F3.boolean.opBoolean","COPY",FACE,{"derivedFrom":makeQuery(id+"F3.opExtrude","CAP_FACE",FACE,{"disambiguationData":[OSD([subQ5,subQ1,subQ6,subQ7,subQ4,subQ3,subQ2,subQ0])],"isStart":false})})}),makeQuery(id+"F8.opExtrude","SWEPT_FACE",FACE,{"disambiguationData":[OSD([sQuery(id+"F7.wireOp",EDGE,"E67")])]})]});}
            var Q5;
            Q5=makeQuery(id+"F8.boolean.opBoolean","INTERSECT",EDGE,{"disambiguationData":[OD(0.0)],"derivedFrom":[makeQuery(id+"F5.opExtrude","SWEPT_FACE",FACE,{"disambiguationData":[OSD([sQuery(id+"F4.wireOp",EDGE,"E30")])]}),makeQuery(id+"F8.opExtrude","SWEPT_FACE",FACE,{"disambiguationData":[OSD([sQuery(id+"F7.wireOp",EDGE,"E67")])]})]});
            fillet(context, id + "F14", {"entities" : qUnion([Q0, Q1, Q2, Q3, Q4, Q5]), "radius" : 3 * mm, "tangentPropagation" : true, "allowEdgeOverflow" : false});
        }
        {
            var Q0;
            Q0=makeQuery(id+"F1.opExtrude","CAP_EDGE",EDGE,{"disambiguationData":[OSD([sQuery(id+"F0.wireOp",EDGE,"E1.bottom")])],"isStart":false});
            fillet(context, id + "F15", {"entities" : qUnion([Q0]), "radius" : 2 * mm, "tangentPropagation" : true, "allowEdgeOverflow" : false});
        }
        {
            var Q0;
            {var subQ0=sQuery(id+"F0.wireOp",EDGE,"E1.bottom");var subQ1=sQuery(id+"F0.wireOp",EDGE,"E1.top");var subQ2=sQuery(id+"F0.wireOp",EDGE,"E1.left");var subQ3=sQuery(id+"F0.wireOp",EDGE,"E1.right");var subQ4=sQuery(id+"F0.wireOp",EDGE,"E4");var subQ5=sQuery(id+"F0.wireOp",EDGE,"E5");var subQ6=sQuery(id+"F0.wireOp",EDGE,"E6");var subQ7=sQuery(id+"F0.wireOp",EDGE,"E7");var subQ8=sQuery(id+"F0.wireOp",EDGE,"E21.filletArc");var subQ9=sQuery(id+"F0.wireOp",EDGE,"E22.filletArc");var subQ10=sQuery(id+"F0.wireOp",EDGE,"E23.filletArc");var subQ11=sQuery(id+"F0.wireOp",EDGE,"E24.filletArc");Q0=makeQuery(id+"F2.boolean.opBoolean","SPLIT",FACE,{"disambiguationData":[TD([makeQuery(id+"F1.opExtrude","SWEPT_FACE",FACE,{"disambiguationData":[OSD([subQ0])]})])],"derivedFrom":makeQuery(id+"F1.opExtrude","CAP_FACE",FACE,{"disambiguationData":[OSD([subQ0,subQ1,subQ2,subQ3,subQ4,subQ5,subQ6,subQ7,subQ8,subQ9,subQ10,subQ11])],"isStart":true})});}
            var sketch = newSketch(context, id + "F16", { "sketchPlane" : qUnion([Q0])});
            skLineSegment(sketch, "E79", {"start": v(94.05, 238.38) * mm, "end": v(94.05, 208.38) * mm, "construction": true});
            skPoint(sketch, "E79.startSnap0", {"position": v(94.05, 208.38) * mm});
            skCircle(sketch, "E80", {"center": v(94.05, 238.38) * mm, "radius": 6 * mm});
            skCircle(sketch, "E81", {"center": v(94.05, 238.38) * mm, "radius": 15 * mm});
            skLineSegment(sketch, "E82", {"start": v(94.05, 238.38) * mm, "end": v(64.05, 208.38) * mm});
            skLineSegment(sketch, "E83", {"start": v(94.05, 238.38) * mm, "end": v(124.05, 208.38) * mm});
            skLineSegment(sketch, "E84", {"start": v(79.05, 238.38) * mm, "end": v(79.05, 223.38) * mm});
            skLineSegment(sketch, "E85", {"start": v(109.05, 238.38) * mm, "end": v(109.05, 223.38) * mm});
            skLineSegment(sketch, "E86", {"start": v(94.05, 28.38) * mm, "end": v(94.05, -1.62) * mm, "construction": true});
            skCircle(sketch, "E87", {"center": v(94.05, -1.62) * mm, "radius": 6 * mm});
            skCircle(sketch, "E88", {"center": v(94.05, -1.62) * mm, "radius": 15 * mm});
            skLineSegment(sketch, "E89", {"start": v(94.05, -1.62) * mm, "end": v(124.05, 28.38) * mm});
            skLineSegment(sketch, "E90", {"start": v(94.05, -1.62) * mm, "end": v(64.05, 28.38) * mm});
            skLineSegment(sketch, "E91", {"start": v(79.05, -1.62) * mm, "end": v(79.05, 13.38) * mm});
            skLineSegment(sketch, "E92", {"start": v(109.05, -1.62) * mm, "end": v(109.05, 13.38) * mm});
            skSolve(sketch);
        }
        {
            var Q0;
            {var subQ0=sQuery(id+"F16.wireOp",EDGE,"E89");var subQ3=sQuery(id+"F16.wireOp",EDGE,"E87");var subQ4=makeQuery(id+"F16.imprint","INTERSECT",VERTEX,{"derivedFrom":[subQ3,subQ0]});Q0=makeQuery(id+"F16.imprint","IMPRINT",FACE,{"disambiguationData":[TD([[makeQuery(id+"F16.imprint","IMPRINT",EDGE,{"disambiguationData":[TD([[subQ4,1.0]])],"derivedFrom":subQ3}),-1.0]])]});}
            var Q1;
            {var subQ0=sQuery(id+"F16.wireOp",EDGE,"E92");Q1=makeQuery(id+"F16.imprint","IMPRINT",FACE,{"disambiguationData":[TD([[makeQuery(id+"F16.imprint","IMPRINT",EDGE,{"derivedFrom":subQ0}),1.0]])]});}
            var Q2;
            {var subQ3=sQuery(id+"F16.wireOp",EDGE,"E91");Q2=makeQuery(id+"F16.imprint","IMPRINT",FACE,{"disambiguationData":[TD([[makeQuery(id+"F16.imprint","IMPRINT",EDGE,{"derivedFrom":subQ3}),-1.0]])]});}
            var Q3;
            {var subQ4=sQuery(id+"F16.wireOp",EDGE,"E88");var subQ6=sQuery(id+"F16.wireOp",EDGE,"E89");var subQ7=makeQuery(id+"F16.imprint","INTERSECT",VERTEX,{"derivedFrom":[subQ4,subQ6]});Q3=makeQuery(id+"F16.imprint","IMPRINT",FACE,{"disambiguationData":[TD([[makeQuery(id+"F16.imprint","IMPRINT",EDGE,{"disambiguationData":[TD([[subQ7,-1.0]])],"derivedFrom":subQ4}),-1.0]])]});}
            var Q4;
            {var subQ3=sQuery(id+"F16.wireOp",EDGE,"E87");var subQ5=sQuery(id+"F16.wireOp",EDGE,"E89");var subQ7=makeQuery(id+"F16.imprint","INTERSECT",VERTEX,{"derivedFrom":[subQ3,subQ5]});Q4=makeQuery(id+"F16.imprint","IMPRINT",FACE,{"disambiguationData":[TD([[makeQuery(id+"F16.imprint","IMPRINT",EDGE,{"disambiguationData":[TD([[subQ7,-1.0]])],"derivedFrom":subQ3}),-1.0]])]});}
            var Q5;
            {var subQ3=sQuery(id+"F16.wireOp",EDGE,"E82");var subQ6=sQuery(id+"F16.wireOp",EDGE,"E81");var subQ8=makeQuery(id+"F16.imprint","INTERSECT",VERTEX,{"derivedFrom":[subQ6,subQ3]});Q5=makeQuery(id+"F16.imprint","IMPRINT",FACE,{"disambiguationData":[TD([[makeQuery(id+"F16.imprint","IMPRINT",EDGE,{"disambiguationData":[TD([[subQ8,-1.0]])],"derivedFrom":subQ6}),-1.0]])]});}
            var Q6;
            {var subQ0=sQuery(id+"F16.wireOp",EDGE,"E82");var subQ3=sQuery(id+"F16.wireOp",EDGE,"E80");var subQ4=makeQuery(id+"F16.imprint","INTERSECT",VERTEX,{"derivedFrom":[subQ3,subQ0]});Q6=makeQuery(id+"F16.imprint","IMPRINT",FACE,{"disambiguationData":[TD([[makeQuery(id+"F16.imprint","IMPRINT",EDGE,{"disambiguationData":[TD([[subQ4,-1.0]])],"derivedFrom":subQ3}),-1.0]])]});}
            var Q7;
            {var subQ0=sQuery(id+"F16.wireOp",EDGE,"E82");var subQ3=sQuery(id+"F16.wireOp",EDGE,"E80");var subQ4=makeQuery(id+"F16.imprint","INTERSECT",VERTEX,{"derivedFrom":[subQ3,subQ0]});Q7=makeQuery(id+"F16.imprint","IMPRINT",FACE,{"disambiguationData":[TD([[makeQuery(id+"F16.imprint","IMPRINT",EDGE,{"disambiguationData":[TD([[subQ4,1.0]])],"derivedFrom":subQ3}),-1.0]])]});}
            var Q8;
            {var subQ3=sQuery(id+"F16.wireOp",EDGE,"E85");Q8=makeQuery(id+"F16.imprint","IMPRINT",FACE,{"disambiguationData":[TD([[makeQuery(id+"F16.imprint","IMPRINT",EDGE,{"derivedFrom":subQ3}),-1.0]])]});}
            var Q9;
            {var subQ0=sQuery(id+"F16.wireOp",EDGE,"E84");Q9=makeQuery(id+"F16.imprint","IMPRINT",FACE,{"disambiguationData":[TD([[makeQuery(id+"F16.imprint","IMPRINT",EDGE,{"derivedFrom":subQ0}),1.0]])]});}
            var Q10;
            Q10=makeQuery(id+"F16.imprint","IMPRINT",FACE,{"disambiguationData":[TD([[makeQuery(id+"F16.imprint","IMPRINT",EDGE,{"derivedFrom":makeQuery(id+"F1.opExtrude","CAP_EDGE",EDGE,{"disambiguationData":[OSD([sQuery(id+"F0.wireOp",EDGE,"E1.left")])],"isStart":true})}),-1.0]])]});
            extrude(context, id + "F17", {"entities" : qUnion([Q0, Q1, Q2, Q3, Q4, Q5, Q6, Q7, Q8, Q9, Q10]), "operationType" : NewBodyOperationType.ADD, "depth" : 3 * mm});
        }
    });
